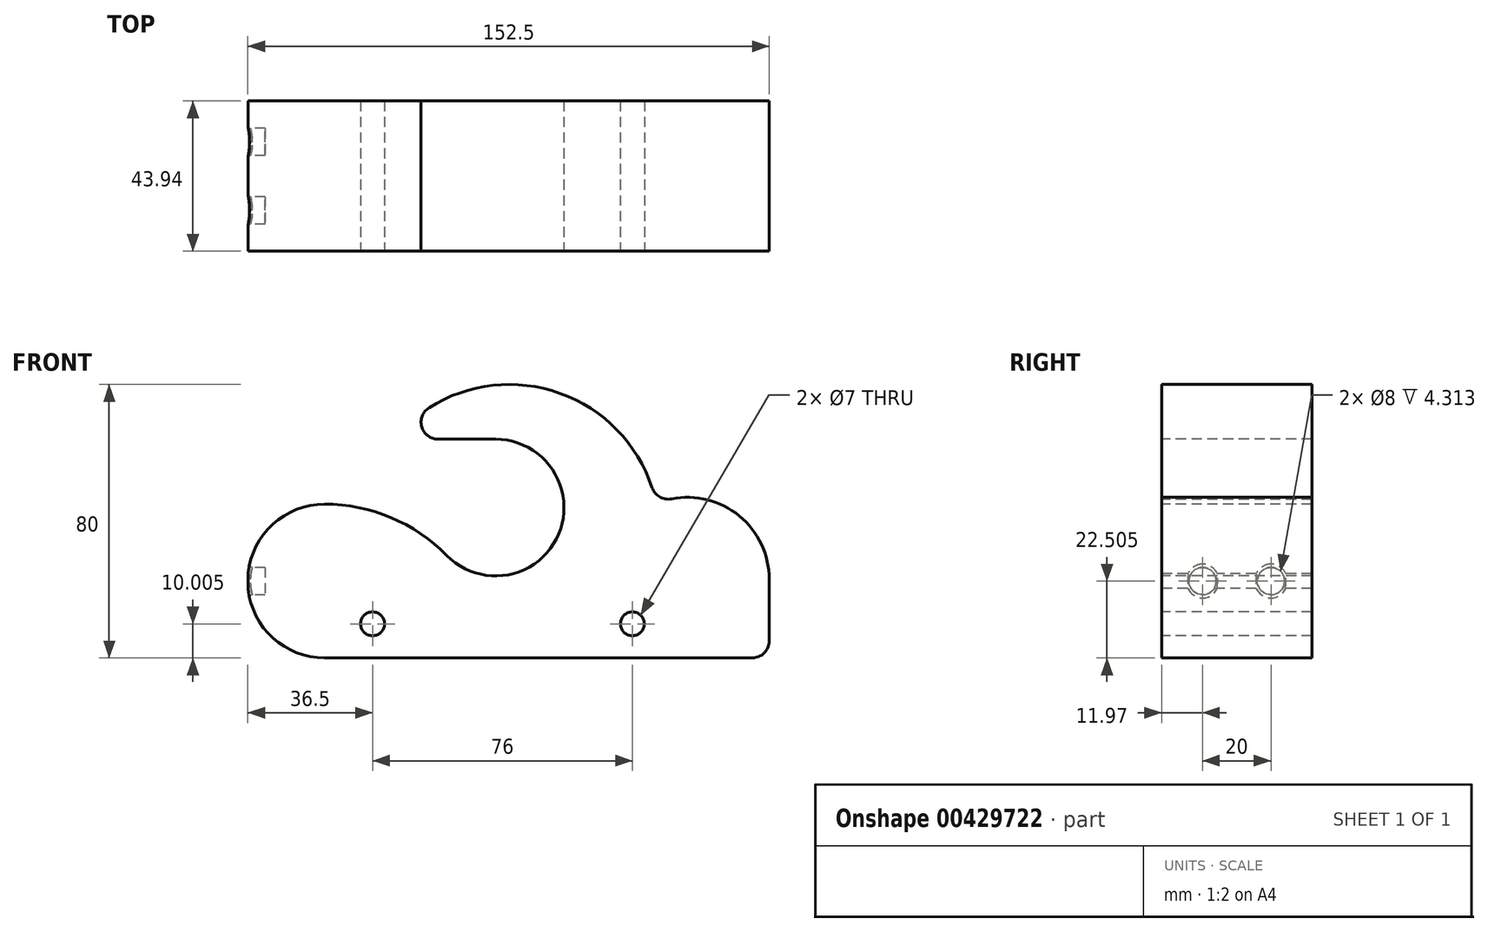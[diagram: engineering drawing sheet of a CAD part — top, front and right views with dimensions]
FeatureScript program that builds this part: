
annotation { "Feature Type Name" : "Feature", "Feature Type Description" : "" }
export const myFeature = defineFeature(function(context is Context, id is Id, definition is map)
    precondition{}
    {
        {
            var Q0;
            Q0=qCreatedBy(makeId("Front.planeOp"),FACE);
            var sketch = newSketch(context, id + "F0", { "sketchPlane" : qUnion([Q0])});
            skLineSegment(sketch, "E0.bottom", {"start": v(76.2, -40) * mm, "end": v(-76.2, -40) * mm});
            skLineSegment(sketch, "E0.top", {"start": v(76.2, 40) * mm, "end": v(-76.2, 40) * mm});
            skLineSegment(sketch, "E0.left", {"start": v(76.2, -40) * mm, "end": v(76.2, 40) * mm});
            skLineSegment(sketch, "E0.right", {"start": v(-76.2, -40) * mm, "end": v(-76.2, 40) * mm});
            skPoint(sketch, "E0.middle", {"position": v(0, 0) * mm});
            skSolve(sketch);
        }
        {
            var Q0;
            Q0 = qSketchRegion(id + "F0", true);
            extrude(context, id + "F1", {"entities" : qUnion([Q0]), "endBound" : BoundingType.SYMMETRIC, "depth" : 43.94 * mm});
        }
        {
            var Q0;
            Q0=makeQuery(id+"F1.opExtrude","CAP_FACE",FACE,{"disambiguationData":[OSD([sQuery(id+"F0.wireOp",EDGE,"E0.bottom"),sQuery(id+"F0.wireOp",EDGE,"E0.top"),sQuery(id+"F0.wireOp",EDGE,"E0.left"),sQuery(id+"F0.wireOp",EDGE,"E0.right")])],"isStart":false});
            var sketch = newSketch(context, id + "F2", { "sketchPlane" : qUnion([Q0])});
            skPoint(sketch, "E1", {"position": v(52.32, -16.9) * mm});
            skArc(sketch, "E2", {"start": v(76.2, -16.9) * mm, "mid": v(67.48, 1.56) * mm, "end": v(47.68, 6.53) * mm});
            skPoint(sketch, "E3", {"position": v(-3.81, 4) * mm});
            skArc(sketch, "E4", {"start": v(-18.1, -10) * mm, "mid": v(14.63, -3.75) * mm, "end": v(-3.82, 24) * mm});
            skPoint(sketch, "E5", {"position": v(-11.89, 4) * mm});
            skPoint(sketch, "E6", {"position": v(0.2, -4) * mm});
            skArc(sketch, "E7", {"start": v(41.96, 9.86) * mm, "mid": v(15.03, 37.42) * mm, "end": v(-23.27, 33.21) * mm});
            skArc(sketch, "E8", {"start": v(41.96, 9.86) * mm, "mid": v(44.19, 7.11) * mm, "end": v(47.68, 6.53) * mm});
            skArc(sketch, "E9", {"start": v(-23.27, 33.21) * mm, "mid": v(-25.4, 27.6) * mm, "end": v(-20.6, 23.99) * mm});
            skLineSegment(sketch, "E10", {"start": v(-20.6, 23.99) * mm, "end": v(-3.82, 24) * mm});
            skArc(sketch, "E11", {"start": v(-18.1, -10) * mm, "mid": v(-34.44, 1.1) * mm, "end": v(-53.8, 5) * mm});
            skArc(sketch, "E12", {"start": v(-53.8, 5) * mm, "mid": v(-76.3, -17.5) * mm, "end": v(-53.8, -40) * mm});
            skLineSegment(sketch, "E13", {"start": v(76.2, -16.9) * mm, "end": v(83.86, -16.9) * mm});
            skLineSegment(sketch, "E14", {"start": v(83.86, -16.9) * mm, "end": v(83.86, 48.6) * mm});
            skLineSegment(sketch, "E15", {"start": v(83.86, 48.6) * mm, "end": v(-81.38, 48.6) * mm});
            skLineSegment(sketch, "E16", {"start": v(-81.38, 48.6) * mm, "end": v(-81.38, -40.77) * mm});
            skLineSegment(sketch, "E17", {"start": v(-81.38, -40.77) * mm, "end": v(-53.8, -40.77) * mm});
            skLineSegment(sketch, "E18", {"start": v(-53.8, -40.77) * mm, "end": v(-53.8, -40) * mm});
            skSolve(sketch);
        }
        {
            var Q0;
            Q0 = qSketchRegion(id + "F2", true);
            extrude(context, id + "F3", {"entities" : qUnion([Q0]), "operationType" : NewBodyOperationType.REMOVE, "endBound" : BoundingType.THROUGH_ALL, "oppositeDirection" : true, "depth" : 25.4 * mm});
        }
        {
            var Q0;
            Q0=makeQuery(id+"F1.opExtrude","SWEPT_EDGE",EDGE,{"disambiguationData":[OSD([sQuery(id+"F0.wireOp",EDGE,"E0.bottom"),sQuery(id+"F0.wireOp",EDGE,"E0.left")])]});
            fillet(context, id + "F4", {"entities" : qUnion([Q0]), "radius" : 5 * mm, "tangentPropagation" : true, "allowEdgeOverflow" : false});
        }
        {
            var Q0;
            Q0=makeQuery(id+"F1.opExtrude","CAP_FACE",FACE,{"disambiguationData":[OSD([sQuery(id+"F0.wireOp",EDGE,"E0.bottom"),sQuery(id+"F0.wireOp",EDGE,"E0.top"),sQuery(id+"F0.wireOp",EDGE,"E0.left"),sQuery(id+"F0.wireOp",EDGE,"E0.right")])],"isStart":false});
            var sketch = newSketch(context, id + "F5", { "sketchPlane" : qUnion([Q0])});
            skPoint(sketch, "E19", {"position": v(-39.8, -30) * mm});
            skPoint(sketch, "E20", {"position": v(36.2, -30) * mm});
            skSolve(sketch);
        }
        {
            var Q0;
            Q0=sQuery(id+"F5.wireOp",VERTEX,"E19");
            var Q1;
            Q1=sQuery(id+"F5.wireOp",VERTEX,"E20");
            var Q2;
            Q2=makeQuery(id+"F1.opExtrude","SWEPT_BODY",BODY,{"disambiguationData":[OSD([sQuery(id+"F0.wireOp",EDGE,"E0.bottom"),sQuery(id+"F0.wireOp",EDGE,"E0.top"),sQuery(id+"F0.wireOp",EDGE,"E0.left"),sQuery(id+"F0.wireOp",EDGE,"E0.right")])]});
            hole(context, id + "F6", {"style" : HoleStyle.SIMPLE, "endStyle" : HoleEndStyle.THROUGH, "standardTappedOrClearance" : lookupTablePath({ "standard" : "ISO", "size" : "7", "type" : "Drilled" }), "standardBlindInLast" : lookupTablePath({ "standard" : "ISO", "size" : "7", "type" : "Drilled" }), "holeDiameter" : 7 * mm, "isTappedThrough" : true, "tappedDepth" : 12.7 * mm, "tapClearance" : 3, "locations" : qUnion([Q0, Q1]), "scope" : qUnion([Q2])});
        }
        {
            var Q0;
            Q0=makeQuery(id+"F1.opExtrude","SWEPT_FACE",FACE,{"disambiguationData":[OSD([sQuery(id+"F0.wireOp",EDGE,"E0.right")])]});
            var sketch = newSketch(context, id + "F7", { "sketchPlane" : qUnion([Q0])});
            skPoint(sketch, "E21", {"position": v(-10, -17.5) * mm});
            skPoint(sketch, "E22", {"position": v(10, -17.5) * mm});
            skCircle(sketch, "E23", {"center": v(-10, -17.5) * mm, "radius": 4 * mm});
            skCircle(sketch, "E24", {"center": v(10, -17.5) * mm, "radius": 4 * mm});
            skSolve(sketch);
        }
        {
            var Q0;
            Q0 = qSketchRegion(id + "F7", true);
            extrude(context, id + "F8", {"entities" : qUnion([Q0]), "operationType" : NewBodyOperationType.REMOVE, "oppositeDirection" : true, "depth" : 5 * mm});
        }
        {
            var Q0;
            {var subQ0=sQuery(id+"F0.wireOp",EDGE,"E0.bottom");Q0=makeQuery(id+"F8.boolean.opBoolean","INTERSECT",EDGE,{"derivedFrom":[makeQuery(id+"F3.boolean.opBoolean","COPY",FACE,{"disambiguationData":[TD([makeQuery(id+"F1.opExtrude","SWEPT_FACE",FACE,{"disambiguationData":[OSD([subQ0])]})])],"derivedFrom":makeQuery(id+"F3.opExtrude","SWEPT_FACE",FACE,{"disambiguationData":[OSD([sQuery(id+"F2.wireOp",EDGE,"E12")])]})}),makeQuery(id+"F8.opExtrude","SWEPT_FACE",FACE,{"disambiguationData":[OSD([sQuery(id+"F7.wireOp",EDGE,"E23")])]})]});}
            var Q1;
            {var subQ0=sQuery(id+"F0.wireOp",EDGE,"E0.bottom");Q1=makeQuery(id+"F8.boolean.opBoolean","INTERSECT",EDGE,{"derivedFrom":[makeQuery(id+"F3.boolean.opBoolean","COPY",FACE,{"disambiguationData":[TD([makeQuery(id+"F1.opExtrude","SWEPT_FACE",FACE,{"disambiguationData":[OSD([subQ0])]})])],"derivedFrom":makeQuery(id+"F3.opExtrude","SWEPT_FACE",FACE,{"disambiguationData":[OSD([sQuery(id+"F2.wireOp",EDGE,"E12")])]})}),makeQuery(id+"F8.opExtrude","SWEPT_FACE",FACE,{"disambiguationData":[OSD([sQuery(id+"F7.wireOp",EDGE,"E24")])]})]});}
            fillet(context, id + "F9", {"entities" : qUnion([Q0, Q1]), "radius" : 0.79 * mm, "tangentPropagation" : true, "allowEdgeOverflow" : false});
        }
    });
